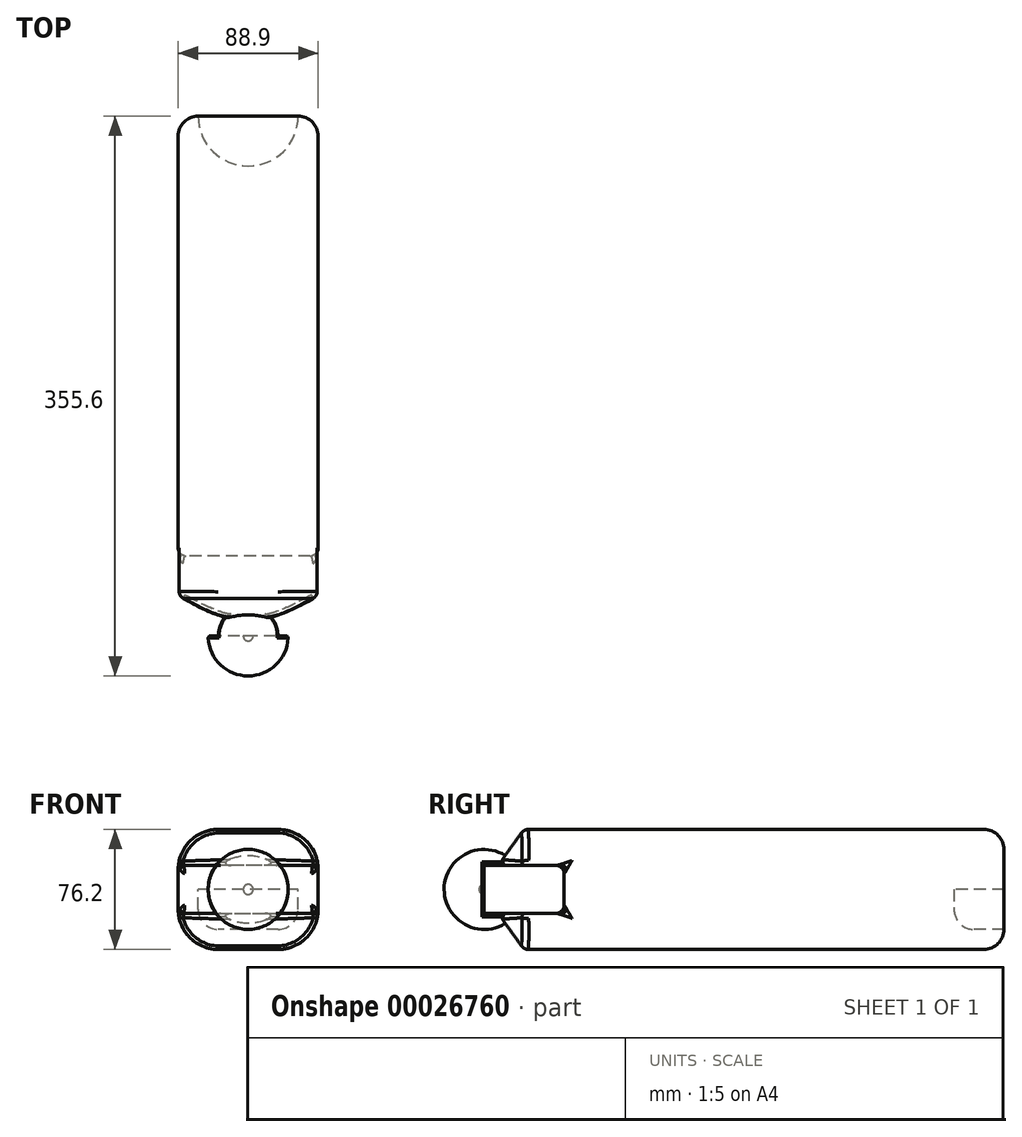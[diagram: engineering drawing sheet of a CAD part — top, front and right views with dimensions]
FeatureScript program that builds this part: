
annotation { "Feature Type Name" : "Feature", "Feature Type Description" : "" }
export const myFeature = defineFeature(function(context is Context, id is Id, definition is map)
    precondition{}
    {
        {
            var Q0;
            Q0=qCreatedBy(makeId("Front.planeOp"),FACE);
            var sketch = newSketch(context, id + "F0", { "sketchPlane" : qUnion([Q0])});
            skLineSegment(sketch, "E0.bottom", {"start": v(-25.4, 0) * mm, "end": v(-63.5, 0) * mm});
            skLineSegment(sketch, "E0.top", {"start": v(-25.4, 76.2) * mm, "end": v(-63.5, 76.2) * mm});
            skLineSegment(sketch, "E0.left", {"start": v(0, 25.4) * mm, "end": v(0, 50.8) * mm});
            skLineSegment(sketch, "E0.right", {"start": v(-88.9, 25.4) * mm, "end": v(-88.9, 50.8) * mm});
            skPoint(sketch, "E1.visualSharp", {"position": v(-88.9, 76.2) * mm});
            skArc(sketch, "E1.filletArc", {"start": v(-63.5, 76.2) * mm, "mid": v(-81.46, 68.76) * mm, "end": v(-88.9, 50.8) * mm});
            skPoint(sketch, "E2.visualSharp", {"position": v(0, 76.2) * mm});
            skArc(sketch, "E2.filletArc", {"start": v(0, 50.8) * mm, "mid": v(-7.44, 68.76) * mm, "end": v(-25.4, 76.2) * mm});
            skPoint(sketch, "E3.visualSharp", {"position": v(0, 0) * mm});
            skArc(sketch, "E3.filletArc", {"start": v(-25.4, 0) * mm, "mid": v(-7.44, 7.44) * mm, "end": v(0, 25.4) * mm});
            skPoint(sketch, "E4.visualSharp", {"position": v(-88.9, 0) * mm});
            skArc(sketch, "E4.filletArc", {"start": v(-88.9, 25.4) * mm, "mid": v(-81.46, 7.44) * mm, "end": v(-63.5, 0) * mm});
            skLineSegment(sketch, "E5", {"start": v(-44.45, 38.1) * mm, "end": v(-44.45, 20.66) * mm});
            skPoint(sketch, "E6.orphan", {"position": v(-44.45, 76.2) * mm});
            skPoint(sketch, "E7.start.orphan", {"position": v(-88.9, 38.1) * mm});
            skCircle(sketch, "E8", {"center": v(-44.45, 38.1) * mm, "radius": 38.1 * mm});
            skSolve(sketch);
        }
        {
            var Q0;
            Q0=makeQuery(id+"F0.imprint","IMPRINT",FACE,{"disambiguationData":[TD([[makeQuery(id+"F0.imprint","IMPRINT",EDGE,{"derivedFrom":sQuery(id+"F0.wireOp",EDGE,"E0.right")}),-1.0]])]});
            var Q1;
            Q1=makeQuery(id+"F0.imprint","IMPRINT",FACE,{"disambiguationData":[TD([[makeQuery(id+"F0.imprint","IMPRINT",EDGE,{"derivedFrom":sQuery(id+"F0.wireOp",EDGE,"E0.left")}),1.0]])]});
            var Q2;
            {var subQ0=sQuery(id+"F0.wireOp",EDGE,"E8");var subQ2=makeQuery(id+"F0.imprint","INTERSECT",VERTEX,{"derivedFrom":[sQuery(id+"F0.wireOp",EDGE,"E0.bottom"),subQ0]});Q2=makeQuery(id+"F0.imprint","IMPRINT",FACE,{"disambiguationData":[TD([[makeQuery(id+"F0.imprint","IMPRINT",EDGE,{"disambiguationData":[TD([[subQ2,1.0]])],"derivedFrom":subQ0}),1.0]])]});}
            extrude(context, id + "F1", {"entities" : qUnion([Q0, Q1, Q2]), "depth" : 304.8 * mm});
        }
        {
            var Q0;
            Q0=makeQuery(id+"F1.opExtrude","CAP_EDGE",EDGE,{"disambiguationData":[OSD([sQuery(id+"F0.wireOp",EDGE,"E0.top")])],"isStart":true});
            fillet(context, id + "F2", {"entities" : qUnion([Q0]), "radius" : 12.7 * mm, "tangentPropagation" : true, "allowEdgeOverflow" : false});
        }
        {
            var Q0;
            Q0=makeQuery(id+"F1.opExtrude","CAP_FACE",FACE,{"disambiguationData":[OSD([sQuery(id+"F0.wireOp",EDGE,"E0.bottom"),sQuery(id+"F0.wireOp",EDGE,"E0.top"),sQuery(id+"F0.wireOp",EDGE,"E0.left"),sQuery(id+"F0.wireOp",EDGE,"E0.right"),sQuery(id+"F0.wireOp",EDGE,"E1.filletArc"),sQuery(id+"F0.wireOp",EDGE,"E2.filletArc"),sQuery(id+"F0.wireOp",EDGE,"E3.filletArc"),sQuery(id+"F0.wireOp",EDGE,"E4.filletArc")])],"isStart":false});
            cPlane(context, id + "F3", {"entities" : qUnion([Q0]), "cplaneType" : CPlaneType.OFFSET, "offset" : 25.4 * mm, "width" : 152.4 * mm, "height" : 152.4 * mm});
        }
        {
            var Q0;
            Q0=qCreatedBy(id+"F3.planeOp",FACE);
            var sketch = newSketch(context, id + "F4", { "sketchPlane" : qUnion([Q0])});
            skCircle(sketch, "E9", {"center": v(-44.45, 38.1) * mm, "radius": 3.18 * mm});
            skPoint(sketch, "E10.end.orphan", {"position": v(-76.2, 38.1) * mm});
            skPoint(sketch, "E11.start.orphan", {"position": v(-44.45, 41.28) * mm});
            skPoint(sketch, "E12.orphan", {"position": v(-44.45, 0) * mm});
            skSolve(sketch);
        }
        {
            var Q1;
            Q1=makeQuery(id+"F1.opExtrude","CAP_FACE",FACE,{"disambiguationData":[OSD([sQuery(id+"F0.wireOp",EDGE,"E0.bottom"),sQuery(id+"F0.wireOp",EDGE,"E0.top"),sQuery(id+"F0.wireOp",EDGE,"E0.left"),sQuery(id+"F0.wireOp",EDGE,"E0.right"),sQuery(id+"F0.wireOp",EDGE,"E1.filletArc"),sQuery(id+"F0.wireOp",EDGE,"E2.filletArc"),sQuery(id+"F0.wireOp",EDGE,"E3.filletArc"),sQuery(id+"F0.wireOp",EDGE,"E4.filletArc")])],"isStart":false});
            var Q2;
            Q2=makeQuery(id+"F4.imprint","IMPRINT",FACE,{"disambiguationData":[TD([[makeQuery(id+"F4.imprint","IMPRINT",EDGE,{"derivedFrom":sQuery(id+"F4.wireOp",EDGE,"E9")}),1.0]])]});
            loft(context, id + "F5", {"operationType" : NewBodyOperationType.ADD, "sheetProfilesArray" : [{ "sheetProfileEntities" : qUnion([Q1]) }, { "sheetProfileEntities" : qUnion([Q2]) }]});
        }
        {
            var Q0;
            {var subQ0=sQuery(id+"F0.wireOp",EDGE,"E0.bottom");Q0=makeQuery(id+"F5.boolean.opBoolean","MERGE",EDGE,{"derivedFrom":[makeQuery(id+"F1.opExtrude","CAP_EDGE",EDGE,{"disambiguationData":[OSD([subQ0])],"isStart":false}),makeQuery(id+"F5.opLoft","MID_CAP_EDGE",EDGE,{"disambiguationData":[OSD([subQ0,sQuery(id+"F0.wireOp",EDGE,"E3.filletArc"),sQuery(id+"F0.wireOp",EDGE,"E4.filletArc")])],"capPos":1.0})]});}
            fillet(context, id + "F6", {"entities" : qUnion([Q0]), "radius" : 5.08 * mm, "tangentPropagation" : true, "allowEdgeOverflow" : false});
        }
        {
            var Q0;
            Q0=makeQuery(id+"F5.opLoft","CAP_FACE",FACE,{"disambiguationData":[OSD([makeQuery(id+"F4.imprint","IMPRINT",FACE,{"disambiguationData":[TD([[makeQuery(id+"F4.imprint","IMPRINT",EDGE,{"derivedFrom":sQuery(id+"F4.wireOp",EDGE,"E9")}),1.0]])]})])],"isStart":true});
            var sketch = newSketch(context, id + "F7", { "sketchPlane" : qUnion([Q0])});
            skCircle(sketch, "E13", {"center": v(-44.45, 38.1) * mm, "radius": 25.4 * mm});
            skPoint(sketch, "E14.orphan", {"position": v(-39.43, 53.16) * mm});
            skPoint(sketch, "E15.end.orphan", {"position": v(-49.47, 23.04) * mm});
            skLineSegment(sketch, "E16", {"start": v(-69.85, 38.1) * mm, "end": v(-19.05, 38.1) * mm});
            skSolve(sketch);
        }
        {
            var Q0;
            {var subQ0=sQuery(id+"F0.wireOp",EDGE,"E0.top");var subQ1=sQuery(id+"F0.wireOp",EDGE,"E1.filletArc");var subQ2=sQuery(id+"F4.wireOp",EDGE,"E9");var subQ6=sQuery(id+"F0.wireOp",EDGE,"E2.filletArc");var subQ7=makeQuery(id+"F5.opLoft","MID_CAP_EDGE",EDGE,{"disambiguationData":[OSD([subQ0,subQ1,subQ6,subQ2])],"capPos":1.0});Q0=makeQuery(id+"F7.imprint","IMPRINT",FACE,{"disambiguationData":[TD([[makeQuery(id+"F7.imprint","IMPRINT",EDGE,{"derivedFrom":subQ7}),-1.0]])]});}
            var Q1;
            Q1=sQuery(id+"F7.wireOp",EDGE,"E16");
            revolve(context, id + "F8", {"operationType" : NewBodyOperationType.ADD, "entities" : qUnion([Q0]), "axis" : qUnion([Q1]), "revolveType" : RevolveType.FULL});
        }
        {
            var Q0;
            {var subQ0=sQuery(id+"F0.wireOp",EDGE,"E0.top");var subQ1=sQuery(id+"F0.wireOp",EDGE,"E1.filletArc");var subQ2=sQuery(id+"F4.wireOp",EDGE,"E9");var subQ6=sQuery(id+"F0.wireOp",EDGE,"E2.filletArc");var subQ7=makeQuery(id+"F5.opLoft","MID_CAP_EDGE",EDGE,{"disambiguationData":[OSD([subQ0,subQ1,subQ6,subQ2])],"capPos":1.0});Q0=makeQuery(id+"F7.imprint","IMPRINT",FACE,{"disambiguationData":[TD([[makeQuery(id+"F7.imprint","IMPRINT",EDGE,{"derivedFrom":subQ7}),1.0]])]});}
            var sketch = newSketch(context, id + "F9", { "sketchPlane" : qUnion([Q0])});
            skLineSegment(sketch, "E17", {"start": v(-44.45, 38.1) * mm, "end": v(-44.45, 53.34) * mm});
            skLineSegment(sketch, "E18", {"start": v(-44.45, 53.34) * mm, "end": v(-90.94, 53.34) * mm});
            skLineSegment(sketch, "E19", {"start": v(-90.94, 53.34) * mm, "end": v(-90.94, 22.86) * mm});
            skLineSegment(sketch, "E20", {"start": v(-90.94, 22.86) * mm, "end": v(1.7, 22.86) * mm});
            skLineSegment(sketch, "E21", {"start": v(1.7, 22.86) * mm, "end": v(1.7, 53.34) * mm});
            skLineSegment(sketch, "E22", {"start": v(1.7, 53.34) * mm, "end": v(-44.45, 53.34) * mm});
            skSolve(sketch);
        }
        {
            var Q0;
            Q0 = qSketchRegion(id + "F9", true);
            extrude(context, id + "F10", {"entities" : qUnion([Q0]), "operationType" : NewBodyOperationType.REMOVE, "oppositeDirection" : true, "depth" : 50.8 * mm});
        }
        {
            var Q0;
            Q0=makeQuery(id+"F10.boolean.opBoolean","INTERSECT",EDGE,{"derivedFrom":[makeQuery(id+"F1.opExtrude","SWEPT_FACE",FACE,{"disambiguationData":[OSD([sQuery(id+"F0.wireOp",EDGE,"E0.right")])]}),makeQuery(id+"F10.opExtrude","CAP_FACE",FACE,{"disambiguationData":[OSD([sQuery(id+"F9.wireOp",EDGE,"E18"),sQuery(id+"F9.wireOp",EDGE,"E19"),sQuery(id+"F9.wireOp",EDGE,"E20"),sQuery(id+"F9.wireOp",EDGE,"E21"),sQuery(id+"F9.wireOp",EDGE,"E22")])],"isStart":false})]});
            fillet(context, id + "F11", {"entities" : qUnion([Q0]), "radius" : 5.08 * mm, "tangentPropagation" : true, "allowEdgeOverflow" : false});
        }
        {
            var Q0;
            Q0=makeQuery(id+"F10.boolean.opBoolean","INTERSECT",EDGE,{"derivedFrom":[makeQuery(id+"F1.opExtrude","SWEPT_FACE",FACE,{"disambiguationData":[OSD([sQuery(id+"F0.wireOp",EDGE,"E1.filletArc")])]}),makeQuery(id+"F10.opExtrude","SWEPT_FACE",FACE,{"disambiguationData":[OSD([sQuery(id+"F9.wireOp",EDGE,"E18"),sQuery(id+"F9.wireOp",EDGE,"E22")])]})]});
            var Q1;
            Q1=makeQuery(id+"F10.boolean.opBoolean","INTERSECT",EDGE,{"derivedFrom":[makeQuery(id+"F1.opExtrude","SWEPT_FACE",FACE,{"disambiguationData":[OSD([sQuery(id+"F0.wireOp",EDGE,"E4.filletArc")])]}),makeQuery(id+"F10.opExtrude","SWEPT_FACE",FACE,{"disambiguationData":[OSD([sQuery(id+"F9.wireOp",EDGE,"E20")])]})]});
            fillet(context, id + "F12", {"entities" : qUnion([Q0, Q1]), "radius" : 2.54 * mm, "tangentPropagation" : true, "allowEdgeOverflow" : false});
        }
        {
            var Q0;
            Q0=makeQuery(id+"F10.boolean.opBoolean","INTERSECT",EDGE,{"derivedFrom":[makeQuery(id+"F1.opExtrude","SWEPT_FACE",FACE,{"disambiguationData":[OSD([sQuery(id+"F0.wireOp",EDGE,"E0.left")])]}),makeQuery(id+"F10.opExtrude","CAP_FACE",FACE,{"disambiguationData":[OSD([sQuery(id+"F9.wireOp",EDGE,"E18"),sQuery(id+"F9.wireOp",EDGE,"E19"),sQuery(id+"F9.wireOp",EDGE,"E20"),sQuery(id+"F9.wireOp",EDGE,"E21"),sQuery(id+"F9.wireOp",EDGE,"E22")])],"isStart":false})]});
            fillet(context, id + "F13", {"entities" : qUnion([Q0]), "radius" : 5.08 * mm, "tangentPropagation" : true, "allowEdgeOverflow" : false});
        }
        {
            var Q0;
            Q0=makeQuery(id+"F10.boolean.opBoolean","INTERSECT",EDGE,{"derivedFrom":[makeQuery(id+"F1.opExtrude","SWEPT_FACE",FACE,{"disambiguationData":[OSD([sQuery(id+"F0.wireOp",EDGE,"E3.filletArc")])]}),makeQuery(id+"F10.opExtrude","SWEPT_FACE",FACE,{"disambiguationData":[OSD([sQuery(id+"F9.wireOp",EDGE,"E20")])]})]});
            var Q1;
            Q1=makeQuery(id+"F10.boolean.opBoolean","INTERSECT",EDGE,{"derivedFrom":[makeQuery(id+"F1.opExtrude","SWEPT_FACE",FACE,{"disambiguationData":[OSD([sQuery(id+"F0.wireOp",EDGE,"E2.filletArc")])]}),makeQuery(id+"F10.opExtrude","SWEPT_FACE",FACE,{"disambiguationData":[OSD([sQuery(id+"F9.wireOp",EDGE,"E18"),sQuery(id+"F9.wireOp",EDGE,"E22")])]})]});
            fillet(context, id + "F14", {"entities" : qUnion([Q0, Q1]), "radius" : 2.54 * mm, "tangentPropagation" : true, "allowEdgeOverflow" : false});
        }
        {
            var Q0;
            Q0=makeQuery(id+"F10.boolean.opBoolean","INTERSECT",EDGE,{"disambiguationData":[OD(1.0)],"derivedFrom":[makeQuery(id+"F8.opRevolve","SWEPT_FACE",FACE,{"disambiguationData":[OSD([sQuery(id+"F7.wireOp",EDGE,"E13")])]}),makeQuery(id+"F10.opExtrude","CAP_FACE",FACE,{"disambiguationData":[OSD([sQuery(id+"F9.wireOp",EDGE,"E18"),sQuery(id+"F9.wireOp",EDGE,"E19"),sQuery(id+"F9.wireOp",EDGE,"E20"),sQuery(id+"F9.wireOp",EDGE,"E21"),sQuery(id+"F9.wireOp",EDGE,"E22")])],"isStart":true})]});
            var Q1;
            Q1=makeQuery(id+"F10.boolean.opBoolean","INTERSECT",EDGE,{"disambiguationData":[OD(1.0)],"derivedFrom":[makeQuery(id+"F8.opRevolve","SWEPT_FACE",FACE,{"disambiguationData":[OSD([sQuery(id+"F7.wireOp",EDGE,"E13")])]}),makeQuery(id+"F10.opExtrude","SWEPT_FACE",FACE,{"disambiguationData":[OSD([sQuery(id+"F9.wireOp",EDGE,"E18"),sQuery(id+"F9.wireOp",EDGE,"E22")])]})]});
            var Q2;
            Q2=makeQuery(id+"F10.boolean.opBoolean","INTERSECT",EDGE,{"disambiguationData":[OD(0.0)],"derivedFrom":[makeQuery(id+"F8.opRevolve","SWEPT_FACE",FACE,{"disambiguationData":[OSD([sQuery(id+"F7.wireOp",EDGE,"E13")])]}),makeQuery(id+"F10.opExtrude","CAP_FACE",FACE,{"disambiguationData":[OSD([sQuery(id+"F9.wireOp",EDGE,"E18"),sQuery(id+"F9.wireOp",EDGE,"E19"),sQuery(id+"F9.wireOp",EDGE,"E20"),sQuery(id+"F9.wireOp",EDGE,"E21"),sQuery(id+"F9.wireOp",EDGE,"E22")])],"isStart":true})]});
            var Q3;
            Q3=makeQuery(id+"F10.boolean.opBoolean","INTERSECT",EDGE,{"disambiguationData":[OD(0.0)],"derivedFrom":[makeQuery(id+"F8.opRevolve","SWEPT_FACE",FACE,{"disambiguationData":[OSD([sQuery(id+"F7.wireOp",EDGE,"E13")])]}),makeQuery(id+"F10.opExtrude","SWEPT_FACE",FACE,{"disambiguationData":[OSD([sQuery(id+"F9.wireOp",EDGE,"E20")])]})]});
            var Q4;
            Q4=makeQuery(id+"F10.boolean.opBoolean","INTERSECT",EDGE,{"disambiguationData":[OD(0.0)],"derivedFrom":[makeQuery(id+"F8.opRevolve","SWEPT_FACE",FACE,{"disambiguationData":[OSD([sQuery(id+"F7.wireOp",EDGE,"E13")])]}),makeQuery(id+"F10.opExtrude","SWEPT_FACE",FACE,{"disambiguationData":[OSD([sQuery(id+"F9.wireOp",EDGE,"E18"),sQuery(id+"F9.wireOp",EDGE,"E22")])]})]});
            var Q5;
            Q5=makeQuery(id+"F10.boolean.opBoolean","INTERSECT",EDGE,{"disambiguationData":[OD(1.0)],"derivedFrom":[makeQuery(id+"F8.opRevolve","SWEPT_FACE",FACE,{"disambiguationData":[OSD([sQuery(id+"F7.wireOp",EDGE,"E13")])]}),makeQuery(id+"F10.opExtrude","SWEPT_FACE",FACE,{"disambiguationData":[OSD([sQuery(id+"F9.wireOp",EDGE,"E20")])]})]});
            fillet(context, id + "F15", {"entities" : qUnion([Q0, Q1, Q2, Q3, Q4, Q5]), "radius" : 1.27 * mm, "tangentPropagation" : true, "allowEdgeOverflow" : false});
        }
        {
            var Q0;
            Q0=makeQuery(id+"F10.boolean.opBoolean","COPY",EDGE,{"derivedFrom":makeQuery(id+"F10.opExtrude","CAP_EDGE",EDGE,{"disambiguationData":[OSD([sQuery(id+"F9.wireOp",EDGE,"E20")])],"isStart":false})});
            var Q1;
            Q1=makeQuery(id+"F10.boolean.opBoolean","COPY",EDGE,{"derivedFrom":makeQuery(id+"F10.opExtrude","CAP_EDGE",EDGE,{"disambiguationData":[OSD([sQuery(id+"F9.wireOp",EDGE,"E18"),sQuery(id+"F9.wireOp",EDGE,"E22")])],"isStart":false})});
            fillet(context, id + "F16", {"entities" : qUnion([Q0, Q1]), "radius" : 5.08 * mm, "tangentPropagation" : true, "allowEdgeOverflow" : false});
        }
        {
            var Q0;
            Q0=makeQuery(id+"F1.opExtrude","CAP_FACE",FACE,{"disambiguationData":[OSD([sQuery(id+"F0.wireOp",EDGE,"E0.bottom"),sQuery(id+"F0.wireOp",EDGE,"E0.top"),sQuery(id+"F0.wireOp",EDGE,"E0.left"),sQuery(id+"F0.wireOp",EDGE,"E0.right"),sQuery(id+"F0.wireOp",EDGE,"E1.filletArc"),sQuery(id+"F0.wireOp",EDGE,"E2.filletArc"),sQuery(id+"F0.wireOp",EDGE,"E3.filletArc"),sQuery(id+"F0.wireOp",EDGE,"E4.filletArc")])],"isStart":true});
            var sketch = newSketch(context, id + "F17", { "sketchPlane" : qUnion([Q0])});
            skLineSegment(sketch, "E23", {"start": v(44.45, 63.5) * mm, "end": v(44.45, 12.7) * mm});
            skLineSegment(sketch, "E24", {"start": v(12.7, 38.1) * mm, "end": v(76.2, 38.1) * mm});
            skCircle(sketch, "E25", {"center": v(44.45, 38.1) * mm, "radius": 9.53 * mm});
            skSolve(sketch);
        }
        {
            var Q0;
            {var subQ0=sQuery(id+"F17.wireOp",EDGE,"E25");var subQ3=sQuery(id+"F17.wireOp",EDGE,"E23");var subQ4=makeQuery(id+"F17.imprint","INTERSECT",VERTEX,{"disambiguationData":[OD(0.0)],"derivedFrom":[subQ3,subQ0]});Q0=makeQuery(id+"F17.imprint","IMPRINT",FACE,{"disambiguationData":[TD([[makeQuery(id+"F17.imprint","IMPRINT",EDGE,{"disambiguationData":[TD([[subQ4,-1.0]])],"derivedFrom":subQ3}),-1.0]])]});}
            var Q1;
            {var subQ1=sQuery(id+"F17.wireOp",EDGE,"E24");var subQ3=sQuery(id+"F17.wireOp",EDGE,"E23");var subQ5=makeQuery(id+"F17.imprint","INTERSECT",VERTEX,{"derivedFrom":[subQ3,subQ1]});Q1=makeQuery(id+"F17.imprint","IMPRINT",FACE,{"disambiguationData":[TD([[makeQuery(id+"F17.imprint","IMPRINT",EDGE,{"disambiguationData":[TD([[subQ5,-1.0]])],"derivedFrom":subQ3}),-1.0]])]});}
            var Q2;
            Q2=sQuery(id+"F17.wireOp",EDGE,"E23");
            revolve(context, id + "F18", {"operationType" : NewBodyOperationType.REMOVE, "entities" : qUnion([Q0, Q1]), "axis" : qUnion([Q2]), "revolveType" : RevolveType.FULL, "oppositeDirection" : true});
        }
    });
